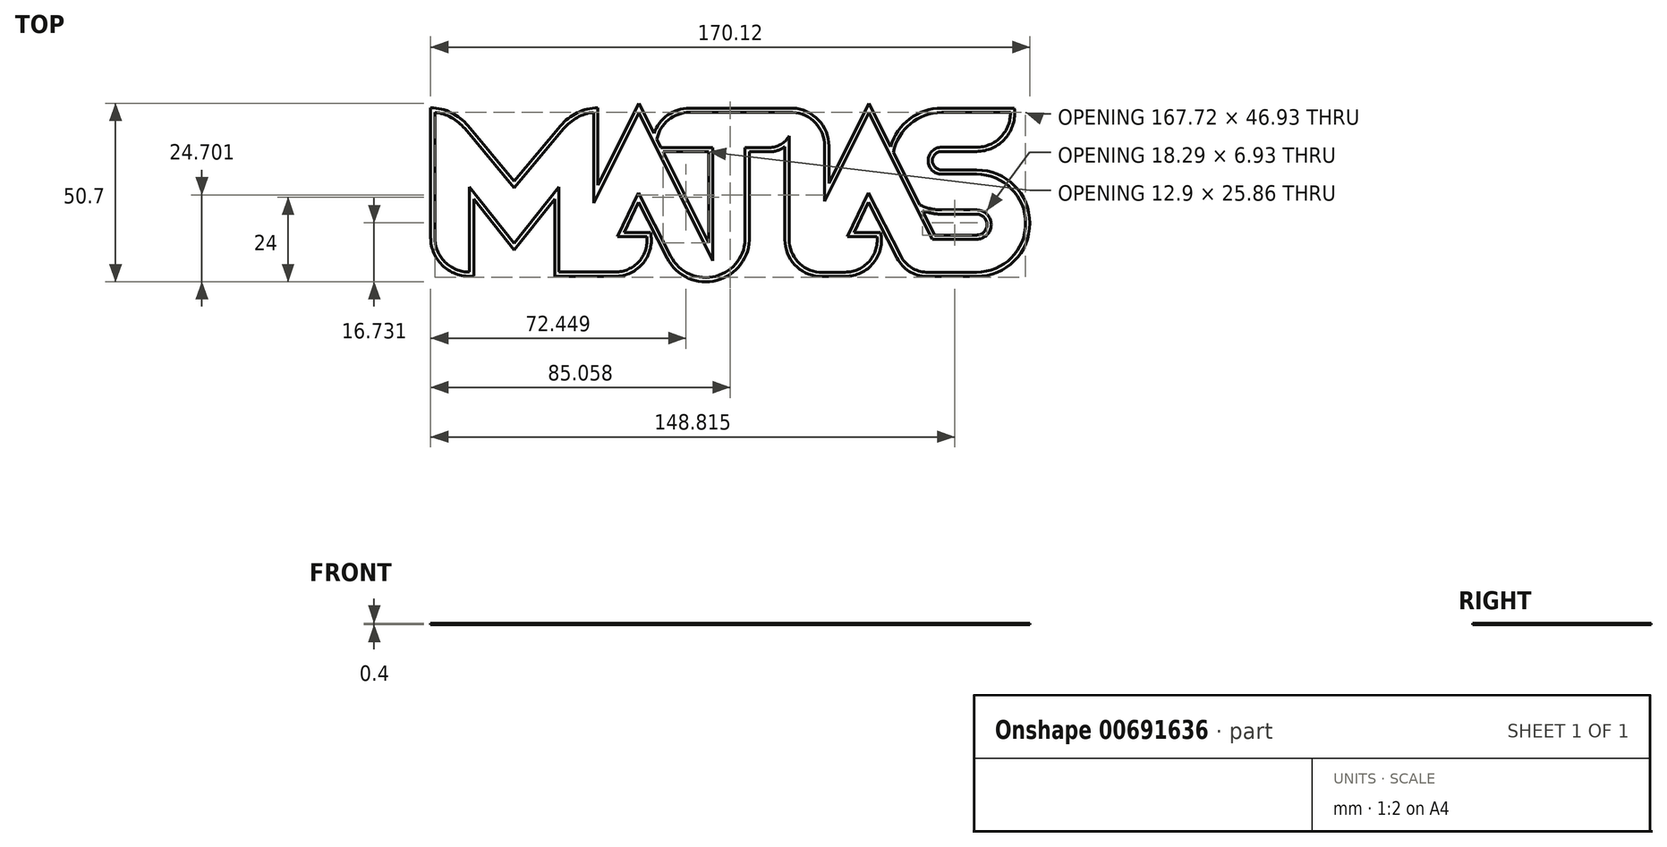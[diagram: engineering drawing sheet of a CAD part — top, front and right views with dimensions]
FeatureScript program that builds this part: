
annotation { "Feature Type Name" : "Feature", "Feature Type Description" : "" }
export const myFeature = defineFeature(function(context is Context, id is Id, definition is map)
    precondition{}
    {
        {
            var Q0;
            Q0=qCreatedBy(makeId("Top.planeOp"),FACE);
            var sketch = newSketch(context, id + "F0", { "sketchPlane" : qUnion([Q0])});
            skLineSegment(sketch, "E0", {"start": v(32.51, 51.2) * mm, "end": v(32.51, 15.58) * mm});
            skLineSegment(sketch, "E1", {"start": v(42.33, 5.78) * mm, "end": v(42.33, 29.93) * mm});
            skLineSegment(sketch, "E2", {"start": v(42.33, 29.93) * mm, "end": v(55.04, 14.01) * mm});
            skArc(sketch, "E3", {"start": v(32.51, 15.58) * mm, "mid": v(35.39, 8.65) * mm, "end": v(42.33, 5.78) * mm});
            skLineSegment(sketch, "E4", {"start": v(40.99, 46.56) * mm, "end": v(55.04, 29.75) * mm});
            skLineSegment(sketch, "E5.MirrorCS", {"start": v(69.1, 46.56) * mm, "end": v(55.04, 29.75) * mm});
            skLineSegment(sketch, "E6.MirrorCS", {"start": v(67.75, 29.93) * mm, "end": v(55.04, 14.01) * mm});
            skLineSegment(sketch, "E7.MirrorCS", {"start": v(77.57, 51.2) * mm, "end": v(77.57, 25.37) * mm});
            skLineSegment(sketch, "E8.MirrorCS", {"start": v(67.75, 5.78) * mm, "end": v(67.75, 29.93) * mm});
            skArc(sketch, "E9.MirrorCS", {"start": v(67.79, 5.78) * mm, "mid": v(67.77, 5.78) * mm, "end": v(67.75, 5.78) * mm});
            skLineSegment(sketch, "E10", {"start": v(90.44, 51.05) * mm, "end": v(77.57, 25.37) * mm});
            skLineSegment(sketch, "E11", {"start": v(67.76, 5.78) * mm, "end": v(83.7, 5.78) * mm});
            skLineSegment(sketch, "E12", {"start": v(92.7, 15.86) * mm, "end": v(84.34, 15.86) * mm});
            skLineSegment(sketch, "E13", {"start": v(84.34, 15.86) * mm, "end": v(90.27, 28.32) * mm});
            skLineSegment(sketch, "E14", {"start": v(90.27, 28.32) * mm, "end": v(99.5, 10.3) * mm});
            skLineSegment(sketch, "E15", {"start": v(111.4, 41.16) * mm, "end": v(111.4, 9) * mm});
            skLineSegment(sketch, "E16", {"start": v(120.59, 15.9) * mm, "end": v(120.59, 41.16) * mm});
            skLineSegment(sketch, "E17", {"start": v(120.59, 41.16) * mm, "end": v(127.47, 41.16) * mm});
            skLineSegment(sketch, "E18", {"start": v(134.09, 51.15) * mm, "end": v(104.8, 51.15) * mm});
            skLineSegment(sketch, "E19", {"start": v(111.4, 41.16) * mm, "end": v(96.71, 41.16) * mm});
            skLineSegment(sketch, "E20", {"start": v(155.77, 51.03) * mm, "end": v(143.2, 25.95) * mm});
            skLineSegment(sketch, "E21", {"start": v(141.56, 5.76) * mm, "end": v(149.04, 5.76) * mm});
            skLineSegment(sketch, "E22", {"start": v(158.03, 15.85) * mm, "end": v(149.67, 15.85) * mm});
            skLineSegment(sketch, "E23", {"start": v(149.67, 15.85) * mm, "end": v(155.6, 28.3) * mm});
            skLineSegment(sketch, "E24", {"start": v(155.6, 28.3) * mm, "end": v(164.83, 10.29) * mm});
            skLineSegment(sketch, "E25", {"start": v(173.7, 15.1) * mm, "end": v(168.21, 26.09) * mm});
            skLineSegment(sketch, "E26", {"start": v(133.1, 51.15) * mm, "end": v(133.1, 51.15) * mm});
            skLineSegment(sketch, "E27", {"start": v(143.2, 25.95) * mm, "end": v(143.2, 41.55) * mm});
            skArc(sketch, "E28", {"start": v(143.2, 41.55) * mm, "mid": v(140.56, 48.17) * mm, "end": v(134.09, 51.15) * mm});
            skArc(sketch, "E29", {"start": v(133.1, 15.02) * mm, "mid": v(135.53, 8.75) * mm, "end": v(141.56, 5.76) * mm});
            skLineSegment(sketch, "E30", {"start": v(173.7, 15.1) * mm, "end": v(186.3, 15.1) * mm});
            skLineSegment(sketch, "E31", {"start": v(186.3, 23.42) * mm, "end": v(176.39, 23.42) * mm});
            skLineSegment(sketch, "E32", {"start": v(176.39, 33.58) * mm, "end": v(186.3, 33.58) * mm});
            skLineSegment(sketch, "E33", {"start": v(176.39, 41.25) * mm, "end": v(186.3, 41.25) * mm});
            skLineSegment(sketch, "E34", {"start": v(195.92, 51.14) * mm, "end": v(176.39, 51.14) * mm});
            skLineSegment(sketch, "E35", {"start": v(186.3, 5.75) * mm, "end": v(178.36, 5.75) * mm});
            skArc(sketch, "E36", {"start": v(186.3, 5.75) * mm, "mid": v(200.23, 19.66) * mm, "end": v(186.3, 33.58) * mm});
            skArc(sketch, "E37", {"start": v(186.3, 15.1) * mm, "mid": v(190.47, 19.26) * mm, "end": v(186.3, 23.42) * mm});
            skArc(sketch, "E38", {"start": v(176.39, 41.25) * mm, "mid": v(172.55, 37.42) * mm, "end": v(176.39, 33.58) * mm});
            skArc(sketch, "E39", {"start": v(176.39, 51.14) * mm, "mid": v(167.5, 47.92) * mm, "end": v(162.74, 39.74) * mm});
            skArc(sketch, "E40", {"start": v(186.3, 41.25) * mm, "mid": v(193.2, 44.17) * mm, "end": v(195.92, 51.14) * mm});
            skLineSegment(sketch, "E41.trimOffspring", {"start": v(111.4, 9) * mm, "end": v(95.37, 41.16) * mm});
            skLineSegment(sketch, "E42.trimOffspring", {"start": v(133.1, 44.48) * mm, "end": v(133.1, 15.02) * mm});
            skPoint(sketch, "E43.orphan", {"position": v(133.1, 5.76) * mm});
            skArc(sketch, "E44.trimOffspring", {"start": v(170.14, 24.9) * mm, "mid": v(173.18, 23.8) * mm, "end": v(176.39, 23.42) * mm});
            skLineSegment(sketch, "E45.trimOffspring", {"start": v(162.53, 37.49) * mm, "end": v(155.77, 51.03) * mm});
            skLineSegment(sketch, "E46", {"start": v(95.37, 41.16) * mm, "end": v(90.44, 51.05) * mm});
            skArc(sketch, "E47", {"start": v(99.5, 10.3) * mm, "mid": v(112.3, 4.6) * mm, "end": v(120.59, 15.9) * mm});
            skArc(sketch, "E48", {"start": v(104.8, 51.15) * mm, "mid": v(98.8, 49) * mm, "end": v(95.53, 43.53) * mm});
            skArc(sketch, "E49", {"start": v(83.7, 5.78) * mm, "mid": v(90.46, 8.8) * mm, "end": v(92.7, 15.86) * mm});
            skArc(sketch, "E50", {"start": v(40.99, 46.56) * mm, "mid": v(37.19, 49.68) * mm, "end": v(32.51, 51.2) * mm});
            skArc(sketch, "E51", {"start": v(77.57, 51.2) * mm, "mid": v(72.9, 49.68) * mm, "end": v(69.1, 46.56) * mm});
            skArc(sketch, "E52", {"start": v(127.47, 41.16) * mm, "mid": v(130.73, 42.05) * mm, "end": v(133.1, 44.48) * mm});
            skArc(sketch, "E53", {"start": v(149.04, 5.76) * mm, "mid": v(155.8, 8.8) * mm, "end": v(158.03, 15.85) * mm});
            skLineSegment(sketch, "E54", {"start": v(178.36, 5.75) * mm, "end": v(172, 5.75) * mm});
            skArc(sketch, "E55", {"start": v(164.83, 10.29) * mm, "mid": v(167.8, 7.04) * mm, "end": v(172, 5.75) * mm});
            skArc(sketch, "E56.0", {"start": v(104.8, 52.35) * mm, "mid": v(98.6, 50.36) * mm, "end": v(94.72, 45.15) * mm});
            skLineSegment(sketch, "E56.1", {"start": v(134.12, 52.35) * mm, "end": v(104.8, 52.35) * mm});
            skArc(sketch, "E56.2", {"start": v(144.4, 41.55) * mm, "mid": v(141.42, 49) * mm, "end": v(134.12, 52.35) * mm});
            skLineSegment(sketch, "E56.3", {"start": v(144.4, 31.02) * mm, "end": v(144.4, 41.55) * mm});
            skLineSegment(sketch, "E56.4", {"start": v(155.77, 53.71) * mm, "end": v(144.4, 31.02) * mm});
            skLineSegment(sketch, "E56.5", {"start": v(161.9, 41.42) * mm, "end": v(155.77, 53.71) * mm});
            skArc(sketch, "E56.6", {"start": v(176.39, 52.34) * mm, "mid": v(167.32, 49.3) * mm, "end": v(161.9, 41.42) * mm});
            skLineSegment(sketch, "E56.7", {"start": v(197.02, 52.34) * mm, "end": v(176.39, 52.34) * mm});
            skArc(sketch, "E56.8", {"start": v(186.3, 40.05) * mm, "mid": v(194.46, 43.76) * mm, "end": v(197.02, 52.34) * mm});
            skLineSegment(sketch, "E56.9", {"start": v(176.39, 40.05) * mm, "end": v(186.3, 40.05) * mm});
            skArc(sketch, "E56.10", {"start": v(176.39, 40.05) * mm, "mid": v(173.75, 37.42) * mm, "end": v(176.39, 34.78) * mm});
            skLineSegment(sketch, "E56.11", {"start": v(94.72, 45.15) * mm, "end": v(90.44, 53.73) * mm});
            skLineSegment(sketch, "E56.12", {"start": v(176.39, 34.78) * mm, "end": v(186.3, 34.78) * mm});
            skArc(sketch, "E56.13", {"start": v(186.3, 4.55) * mm, "mid": v(201.43, 19.66) * mm, "end": v(186.3, 34.78) * mm});
            skLineSegment(sketch, "E56.14", {"start": v(186.3, 4.55) * mm, "end": v(178.36, 4.55) * mm});
            skLineSegment(sketch, "E56.15", {"start": v(178.36, 4.55) * mm, "end": v(171.97, 4.55) * mm});
            skArc(sketch, "E56.16", {"start": v(163.76, 9.74) * mm, "mid": v(167.16, 6.02) * mm, "end": v(171.97, 4.55) * mm});
            skLineSegment(sketch, "E56.17", {"start": v(155.64, 25.6) * mm, "end": v(163.76, 9.74) * mm});
            skLineSegment(sketch, "E56.18", {"start": v(151.57, 17.05) * mm, "end": v(155.64, 25.6) * mm});
            skLineSegment(sketch, "E56.19", {"start": v(159.04, 17.05) * mm, "end": v(151.57, 17.05) * mm});
            skArc(sketch, "E56.20", {"start": v(149.04, 4.56) * mm, "mid": v(157.04, 8.4) * mm, "end": v(159.04, 17.05) * mm});
            skLineSegment(sketch, "E56.21", {"start": v(141.51, 4.56) * mm, "end": v(149.04, 4.56) * mm});
            skArc(sketch, "E56.22", {"start": v(131.9, 15.02) * mm, "mid": v(134.66, 7.92) * mm, "end": v(141.51, 4.56) * mm});
            skLineSegment(sketch, "E56.23", {"start": v(43.53, 26.5) * mm, "end": v(55.04, 12.1) * mm});
            skLineSegment(sketch, "E56.24", {"start": v(43.53, 4.65) * mm, "end": v(43.53, 26.5) * mm});
            skArc(sketch, "E56.25", {"start": v(31.31, 15.58) * mm, "mid": v(34.98, 7.39) * mm, "end": v(43.53, 4.65) * mm});
            skLineSegment(sketch, "E56.26", {"start": v(31.31, 52.5) * mm, "end": v(31.31, 15.58) * mm});
            skArc(sketch, "E56.27", {"start": v(41.9, 47.33) * mm, "mid": v(37.16, 51.04) * mm, "end": v(31.31, 52.5) * mm});
            skLineSegment(sketch, "E56.28", {"start": v(41.9, 47.33) * mm, "end": v(55.04, 31.62) * mm});
            skLineSegment(sketch, "E56.29", {"start": v(90.44, 53.73) * mm, "end": v(78.77, 30.45) * mm});
            skLineSegment(sketch, "E56.30", {"start": v(78.77, 52.5) * mm, "end": v(78.77, 30.45) * mm});
            skArc(sketch, "E56.31", {"start": v(78.77, 52.5) * mm, "mid": v(72.92, 51.04) * mm, "end": v(68.18, 47.33) * mm});
            skLineSegment(sketch, "E56.32", {"start": v(68.18, 47.33) * mm, "end": v(55.04, 31.62) * mm});
            skLineSegment(sketch, "E56.33", {"start": v(66.55, 26.5) * mm, "end": v(55.04, 12.1) * mm});
            skLineSegment(sketch, "E56.34", {"start": v(66.55, 4.58) * mm, "end": v(66.55, 26.5) * mm});
            skLineSegment(sketch, "E56.35", {"start": v(66.55, 4.58) * mm, "end": v(83.7, 4.58) * mm});
            skArc(sketch, "E56.36", {"start": v(83.7, 4.58) * mm, "mid": v(91.7, 8.42) * mm, "end": v(93.7, 17.06) * mm});
            skLineSegment(sketch, "E56.37", {"start": v(93.7, 17.06) * mm, "end": v(86.24, 17.06) * mm});
            skLineSegment(sketch, "E56.38", {"start": v(86.24, 17.06) * mm, "end": v(90.3, 25.6) * mm});
            skLineSegment(sketch, "E56.39", {"start": v(90.3, 25.6) * mm, "end": v(98.43, 9.76) * mm});
            skArc(sketch, "E56.40", {"start": v(98.43, 9.76) * mm, "mid": v(112.59, 3.44) * mm, "end": v(121.79, 15.92) * mm});
            skLineSegment(sketch, "E56.41", {"start": v(121.79, 15.92) * mm, "end": v(121.79, 39.96) * mm});
            skLineSegment(sketch, "E56.42", {"start": v(121.79, 39.96) * mm, "end": v(127.47, 39.96) * mm});
            skArc(sketch, "E56.43", {"start": v(127.47, 39.96) * mm, "mid": v(129.79, 40.32) * mm, "end": v(131.9, 41.37) * mm});
            skLineSegment(sketch, "E56.44", {"start": v(131.9, 41.37) * mm, "end": v(131.9, 15.02) * mm});
            skLineSegment(sketch, "E57.0", {"start": v(110.2, 14.1) * mm, "end": v(97.3, 39.96) * mm});
            skLineSegment(sketch, "E57.1", {"start": v(110.2, 39.96) * mm, "end": v(110.2, 14.1) * mm});
            skLineSegment(sketch, "E57.2", {"start": v(110.2, 39.96) * mm, "end": v(97.3, 39.96) * mm});
            skArc(sketch, "E58.0", {"start": v(170.98, 23.22) * mm, "mid": v(173.64, 22.47) * mm, "end": v(176.39, 22.22) * mm});
            skLineSegment(sketch, "E58.1", {"start": v(174.44, 16.3) * mm, "end": v(170.98, 23.22) * mm});
            skLineSegment(sketch, "E58.2", {"start": v(186.3, 22.22) * mm, "end": v(176.39, 22.22) * mm});
            skArc(sketch, "E58.3", {"start": v(186.3, 16.3) * mm, "mid": v(189.27, 19.26) * mm, "end": v(186.3, 22.22) * mm});
            skLineSegment(sketch, "E58.4", {"start": v(174.44, 16.3) * mm, "end": v(186.3, 16.3) * mm});
            skLineSegment(sketch, "E59", {"start": v(96.71, 41.16) * mm, "end": v(95.53, 43.53) * mm});
            skLineSegment(sketch, "E60", {"start": v(168.21, 26.09) * mm, "end": v(162.53, 37.49) * mm});
            skLineSegment(sketch, "E61", {"start": v(162.74, 39.74) * mm, "end": v(170.14, 24.9) * mm});
            skSolve(sketch);
        }
        {
            var Q0;
            Q0=makeQuery(id+"F0.imprint","IMPRINT",FACE,{"disambiguationData":[TD([[makeQuery(id+"F0.imprint","IMPRINT",EDGE,{"derivedFrom":sQuery(id+"F0.wireOp",EDGE,"E0")}),-1.0]])]});
            extrude(context, id + "F1", {"entities" : qUnion([Q0]), "depth" : 0.4 * mm, "offsetDistance" : 25 * mm});
        }
    });
